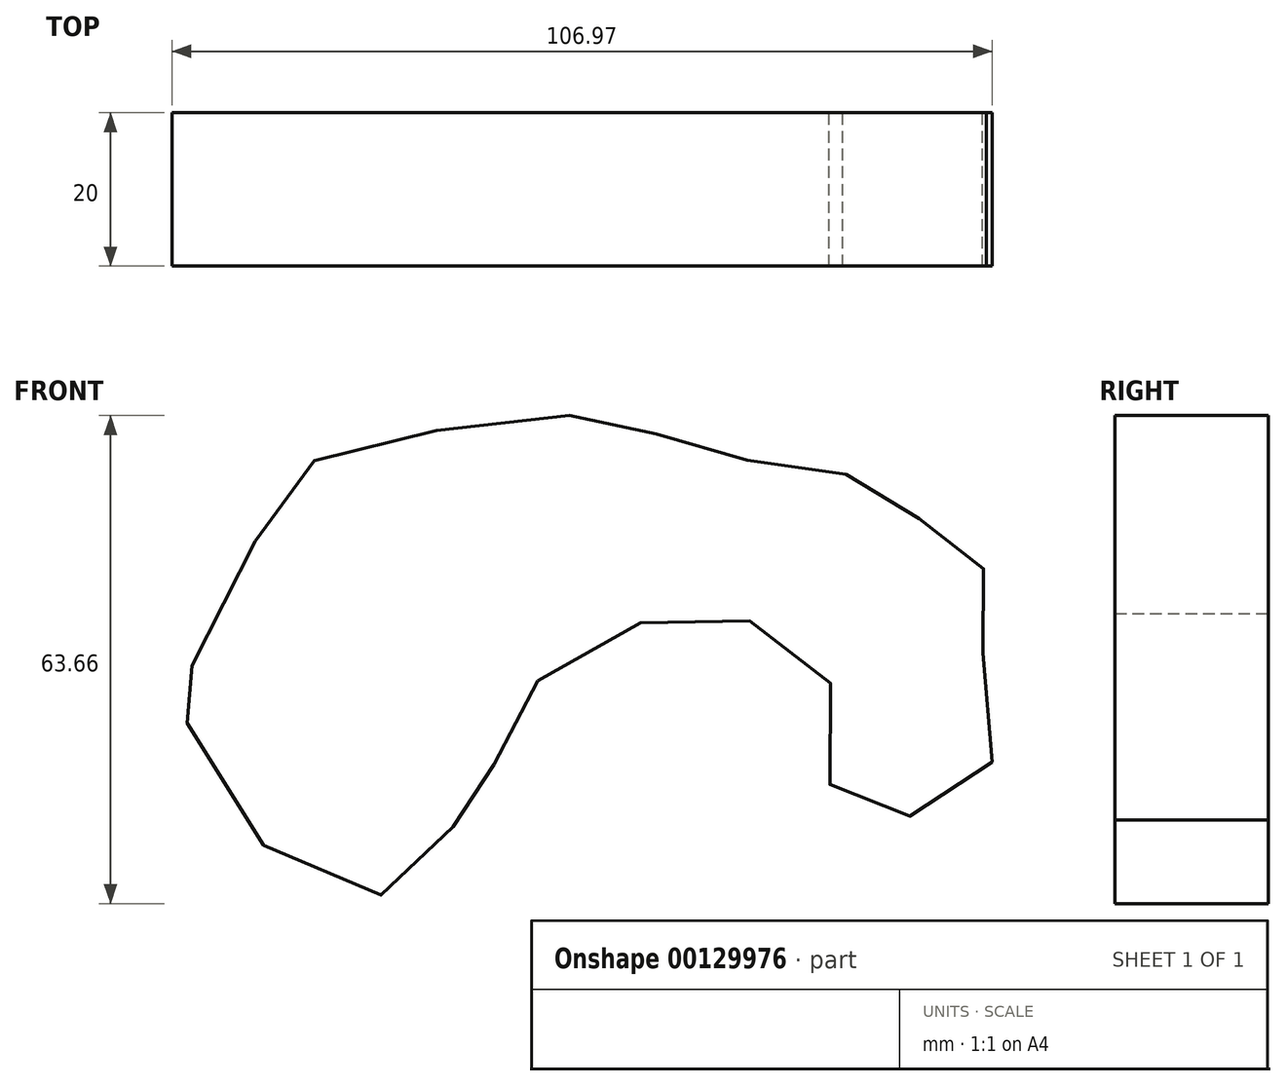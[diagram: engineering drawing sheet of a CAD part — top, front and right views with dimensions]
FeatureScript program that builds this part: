
annotation { "Feature Type Name" : "Feature", "Feature Type Description" : "" }
export const myFeature = defineFeature(function(context is Context, id is Id, definition is map)
    precondition{}
    {
        {
            var Q0;
            Q0=qCreatedBy(makeId("Front.planeOp"),FACE);
            var sketch = newSketch(context, id + "F0", { "sketchPlane" : qUnion([Q0])});
            skFitSpline(sketch, "E0", {"points": [v(-27.77, 36.7) * mm, v(-46.22, 31.14) * mm, v(-53.76, 16.86) * mm, v(-62.29, 0) * mm, v(-59.9, -1.79) * mm, v(-42.45, -24.6) * mm, v(-26.38, -16.86) * mm, v(-25.2, -13.3) * mm, v(-19.04, -4.96) * mm, v(-13.49, 5.36) * mm, v(4.76, 12.7) * mm, v(17.46, 9.72) * mm, v(25.2, -1.59) * mm, v(24.2, -12.9) * mm, v(43.24, -10.12) * mm, v(43.84, -1.98) * mm, v(43.84, 15.27) * mm, v(43.04, 19.44) * mm, v(35.11, 25.2) * mm, v(26.98, 30.55) * mm, v(14.48, 32.53) * mm, v(2.18, 35.7) * mm, v(-6.35, 38.48) * mm, v(-27.77, 36.7) * mm]});
            skSolve(sketch);
        }
        {
            var Q0;
            Q0 = qSketchRegion(id + "F0", true);
            var Q1;
            Q1=makeQuery(id+"F0.imprint","IMPRINT",FACE,{"disambiguationData":[TD([[makeQuery(id+"F0.imprint","IMPRINT",EDGE,{"derivedFrom":sQuery(id+"F0.wireOp",EDGE,"E0")}),1.0]])]});
            extrude(context, id + "F1", {"entities" : qUnion([Q0, Q1]), "depth" : 20 * mm});
        }
    });
